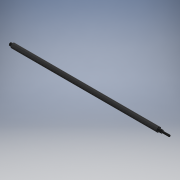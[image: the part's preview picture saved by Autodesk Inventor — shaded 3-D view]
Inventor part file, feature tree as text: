
AUTODESK INVENTOR PART (.ipt)
format: ipt  version: 2017.1 (Build 211199000, 199)  size: 147,456 bytes
history: native  units: mm
features: sketch x4, revolve x3, thread x1, extrude x1
ambient origin geometry x8: Origin, YZ Plane, XZ Plane, XY Plane, X Axis, Y Axis, Z Axis, Center Point
bodies: Solid1 (feature_tree)
feature tree (9):
  revolve  "Revolution1"  [1 undecoded]
  thread  "Thread1"  [1 undecoded]
  revolve  "Revolution2"  [1 undecoded]
  revolve  "Revolution3"  [1 undecoded]
  extrude  "Extrusion1"  [1 undecoded]
  sketch  "Sketch_16"
  sketch  "Sketch_23"
  sketch  "Sketch_4"  dims[d0=360.0deg d1=384.0mm d2=0.0mm d3=360.0deg]
  sketch  "Sketch_8"  dims[d4=360.0deg d5=7.0mm d6=0.0mm]
note: 5 required parameter values undecoded (feature->parameter linkage not recoverable at this tier; creation-order binding heuristic only, values carry confidence <= 0.55)